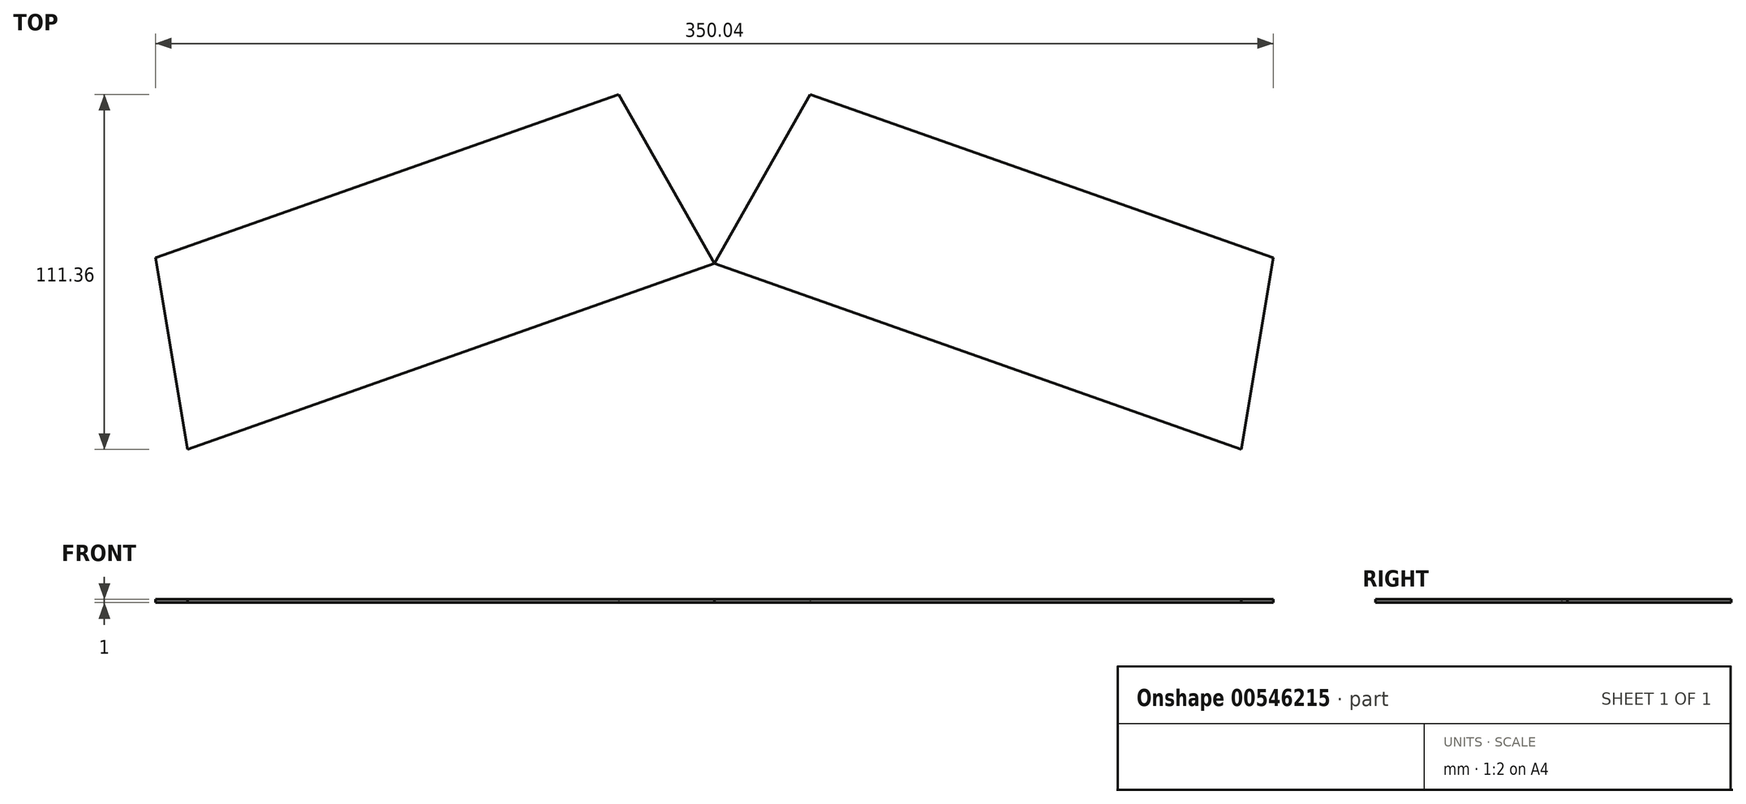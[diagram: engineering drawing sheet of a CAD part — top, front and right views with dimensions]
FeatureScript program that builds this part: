
annotation { "Feature Type Name" : "Feature", "Feature Type Description" : "" }
export const myFeature = defineFeature(function(context is Context, id is Id, definition is map)
    precondition{}
    {
        {
            var Q0;
            Q0=qCreatedBy(makeId("Top.planeOp"),FACE);
            var sketch = newSketch(context, id + "F0", { "sketchPlane" : qUnion([Q0])});
            skLineSegment(sketch, "E0.bottom", {"start": v(-225, 148.5) * mm, "end": v(15, 148.5) * mm, "construction": true});
            skLineSegment(sketch, "E0.top", {"start": v(-225, -148.5) * mm, "end": v(15, -148.5) * mm, "construction": true});
            skLineSegment(sketch, "E0.left", {"start": v(-225, 148.5) * mm, "end": v(-225, -148.5) * mm, "construction": true});
            skLineSegment(sketch, "E0.right", {"start": v(15, 148.5) * mm, "end": v(15, -148.5) * mm, "construction": true});
            skLineSegment(sketch, "E1", {"start": v(-15, 148.5) * mm, "end": v(-15, -148.5) * mm, "construction": true});
            skLineSegment(sketch, "E2", {"start": v(0, 148.5) * mm, "end": v(0, -148.5) * mm, "construction": true});
            skSolve(sketch);
        }
        {
            var Q0;
            Q0=qCreatedBy(makeId("Top.planeOp"),FACE);
            var sketch = newSketch(context, id + "F1", { "sketchPlane" : qUnion([Q0])});
            skLineSegment(sketch, "E3", {"start": v(-165, 30.2) * mm, "end": v(0, 88.5) * mm});
            skLineSegment(sketch, "E4", {"start": v(-165, 30.2) * mm, "end": v(-175.02, 90.29) * mm});
            skLineSegment(sketch, "E5", {"start": v(-175.02, 90.29) * mm, "end": v(-29.97, 141.55) * mm});
            skLineSegment(sketch, "E6", {"start": v(-29.97, 141.55) * mm, "end": v(0, 88.5) * mm});
            skSolve(sketch);
        }
        {
            var Q0;
            Q0=qSketchRegion(id+"F1",true);
            extrude(context, id + "F2", {"entities" : qUnion([Q0]), "depth" : 1 * mm, "offsetDistance" : 25 * mm});
        }
        {
            var Q0;
            Q0=makeQuery(id+"F2.opExtrude","SWEPT_BODY",BODY,{"disambiguationData":[OSD([sQuery(id+"F1.wireOp",EDGE,"E3"),sQuery(id+"F1.wireOp",EDGE,"E4"),sQuery(id+"F1.wireOp",EDGE,"E5"),sQuery(id+"F1.wireOp",EDGE,"E6")])]});
            var Q1;
            Q1=qCreatedBy(makeId("Right.planeOp"),FACE);
            mirror(context, id + "F3", {"entities" : qUnion([Q0]), "mirrorPlane" : qUnion([Q1])});
        }
    });
